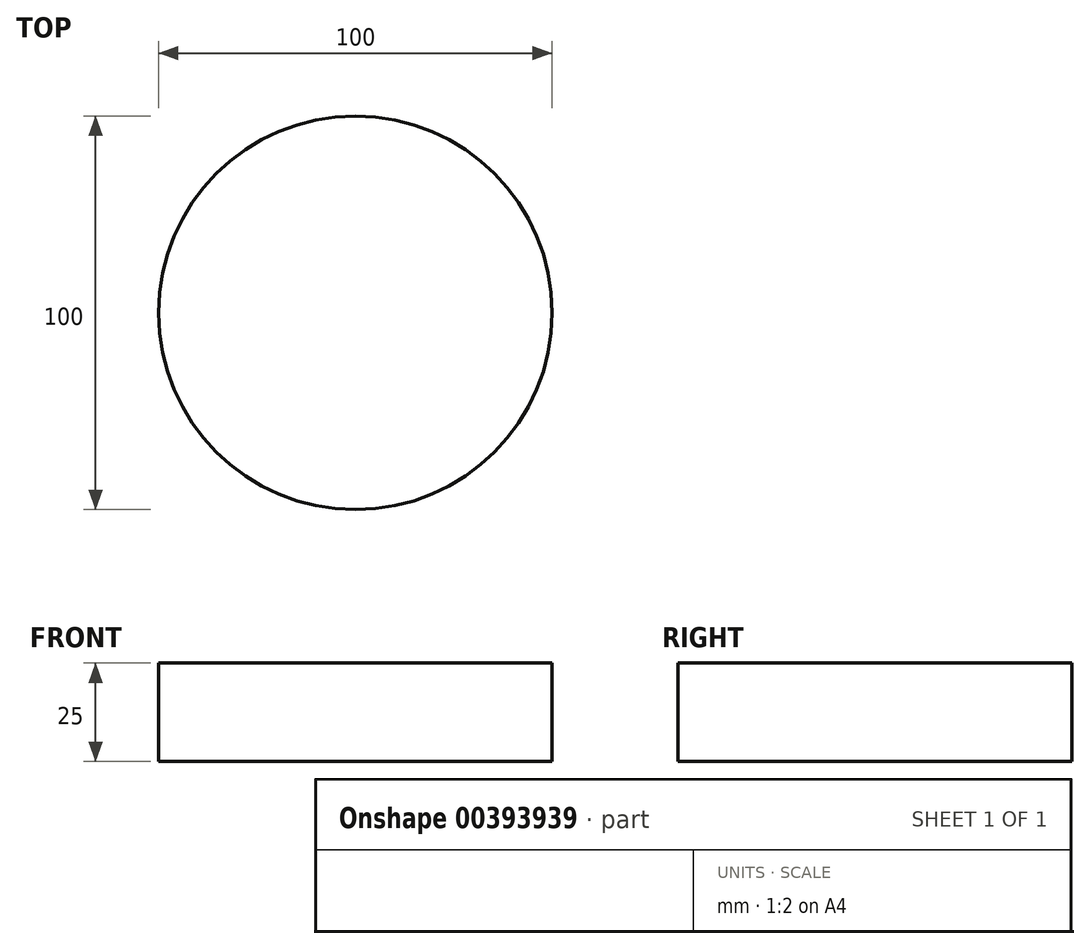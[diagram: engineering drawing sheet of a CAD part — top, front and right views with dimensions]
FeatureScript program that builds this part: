
annotation { "Feature Type Name" : "Feature", "Feature Type Description" : "" }
export const myFeature = defineFeature(function(context is Context, id is Id, definition is map)
    precondition{}
    {
        {
            var Q0;
            Q0=qCreatedBy(makeId("Top.planeOp"),FACE);
            var sketch = newSketch(context, id + "F0", { "sketchPlane" : qUnion([Q0])});
            skCircle(sketch, "E0", {"center": v(0, 0) * mm, "radius": 50 * mm});
            skSolve(sketch);
        }
        {
            var Q0;
            Q0=makeQuery(id+"F0.imprint","IMPRINT",FACE,{"disambiguationData":[TD([[makeQuery(id+"F0.imprint","IMPRINT",EDGE,{"derivedFrom":sQuery(id+"F0.wireOp",EDGE,"E0")}),1.0]])]});
            extrude(context, id + "F1", {"entities" : qUnion([Q0]), "depth" : 25 * mm, "offsetDistance" : 25 * mm});
        }
    });
